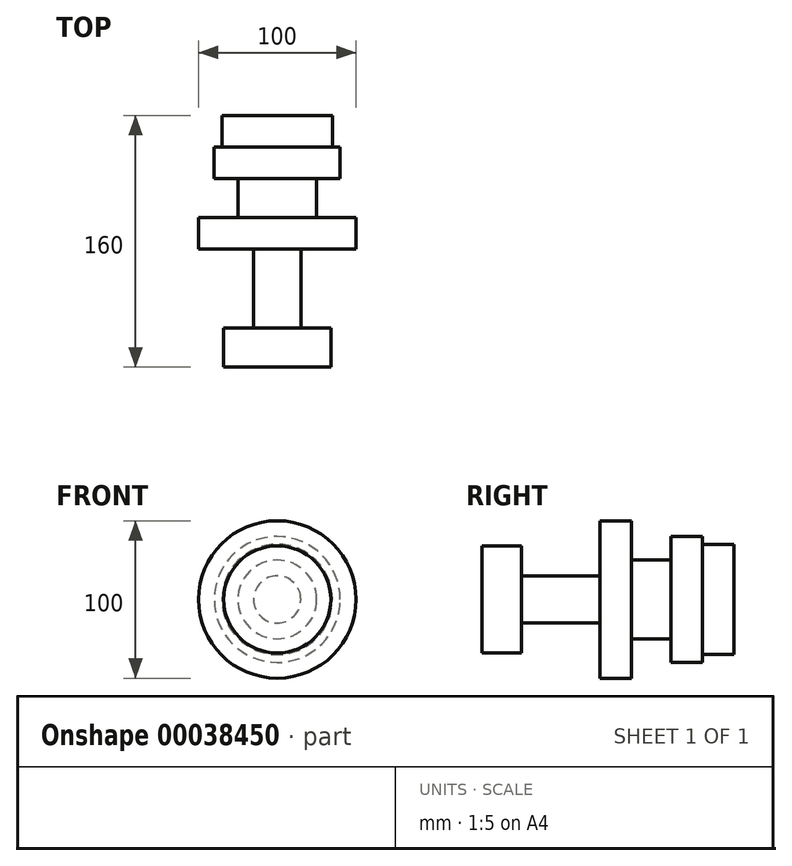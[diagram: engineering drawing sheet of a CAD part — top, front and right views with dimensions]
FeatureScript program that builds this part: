
annotation { "Feature Type Name" : "Feature", "Feature Type Description" : "" }
export const myFeature = defineFeature(function(context is Context, id is Id, definition is map)
    precondition{}
    {
        {
            var Q0;
            Q0=qCreatedBy(makeId("Front.planeOp"),FACE);
            var sketch = newSketch(context, id + "F0", { "sketchPlane" : qUnion([Q0])});
            skCircle(sketch, "E0", {"center": v(0, 0) * mm, "radius": 35 * mm});
            skSolve(sketch);
        }
        {
            var Q0;
            Q0=qSketchRegion(id+"F0",true);
            extrude(context, id + "F1", {"entities" : qUnion([Q0]), "depth" : 20 * mm});
        }
        {
            var Q0;
            Q0=makeQuery(id+"F1.opExtrude","CAP_FACE",FACE,{"disambiguationData":[OSD([sQuery(id+"F0.wireOp",EDGE,"E0")])],"isStart":false});
            var sketch = newSketch(context, id + "F2", { "sketchPlane" : qUnion([Q0])});
            skCircle(sketch, "E1", {"center": v(0, 0) * mm, "radius": 40 * mm});
            skSolve(sketch);
        }
        {
            var Q0;
            Q0=makeQuery(id+"F2.imprint","IMPRINT",FACE,{"disambiguationData":[TD([[makeQuery(id+"F2.imprint","IMPRINT",EDGE,{"derivedFrom":sQuery(id+"F2.wireOp",EDGE,"E1")}),1.0]])]});
            var Q1;
            Q1=makeQuery(id+"F2.imprint","IMPRINT",FACE,{"disambiguationData":[TD([[makeQuery(id+"F2.imprint","IMPRINT",EDGE,{"derivedFrom":makeQuery(id+"F1.opExtrude","CAP_EDGE",EDGE,{"disambiguationData":[OSD([sQuery(id+"F0.wireOp",EDGE,"E0")])],"isStart":false})}),1.0]])]});
            var Q2;
            Q2=sQuery(id+"F2.wireOp",EDGE,"E1");
            extrude(context, id + "F3", {"entities" : qUnion([Q0, Q1]), "surfaceEntities" : qUnion([Q2]), "depth" : 20 * mm});
        }
        {
            var Q0;
            Q0=makeQuery(id+"F3.opExtrude","CAP_FACE",FACE,{"disambiguationData":[OSD([sQuery(id+"F2.wireOp",EDGE,"E1")])],"isStart":false});
            var sketch = newSketch(context, id + "F4", { "sketchPlane" : qUnion([Q0])});
            skCircle(sketch, "E2", {"center": v(0, 0) * mm, "radius": 25 * mm});
            skSolve(sketch);
        }
        {
            var Q0;
            Q0=makeQuery(id+"F4.imprint","IMPRINT",FACE,{"disambiguationData":[TD([[makeQuery(id+"F4.imprint","IMPRINT",EDGE,{"derivedFrom":sQuery(id+"F4.wireOp",EDGE,"E2")}),1.0]])]});
            var Q1;
            Q1=sQuery(id+"F4.wireOp",EDGE,"E2");
            extrude(context, id + "F5", {"entities" : qUnion([Q0]), "operationType" : NewBodyOperationType.ADD, "surfaceEntities" : qUnion([Q1]), "depth" : 25 * mm});
        }
        {
            var Q0;
            Q0=makeQuery(id+"F5.opExtrude","CAP_FACE",FACE,{"disambiguationData":[OSD([sQuery(id+"F4.wireOp",EDGE,"E2")])],"isStart":false});
            var sketch = newSketch(context, id + "F6", { "sketchPlane" : qUnion([Q0])});
            skCircle(sketch, "E3", {"center": v(0, 0) * mm, "radius": 50 * mm});
            skSolve(sketch);
        }
        {
            var Q0;
            Q0=qSketchRegion(id+"F6",true);
            extrude(context, id + "F7", {"entities" : qUnion([Q0]), "operationType" : NewBodyOperationType.ADD, "depth" : 20 * mm});
        }
        {
            var Q0;
            Q0=makeQuery(id+"F7.opExtrude","CAP_FACE",FACE,{"disambiguationData":[OSD([sQuery(id+"F6.wireOp",EDGE,"E3")])],"isStart":false});
            var sketch = newSketch(context, id + "F8", { "sketchPlane" : qUnion([Q0])});
            skCircle(sketch, "E4", {"center": v(0, 0) * mm, "radius": 15 * mm});
            skSolve(sketch);
        }
        {
            var Q0;
            Q0=qSketchRegion(id+"F8",true);
            extrude(context, id + "F9", {"entities" : qUnion([Q0]), "operationType" : NewBodyOperationType.ADD, "depth" : 50 * mm});
        }
        {
            var Q0;
            Q0=makeQuery(id+"F9.opExtrude","CAP_FACE",FACE,{"disambiguationData":[OSD([sQuery(id+"F8.wireOp",EDGE,"E4")])],"isStart":false});
            var sketch = newSketch(context, id + "F10", { "sketchPlane" : qUnion([Q0])});
            skCircle(sketch, "E5", {"center": v(0, 0) * mm, "radius": 34.03 * mm});
            skSolve(sketch);
        }
        {
            var Q0;
            Q0=makeQuery(id+"F10.imprint","IMPRINT",FACE,{"disambiguationData":[TD([[makeQuery(id+"F10.imprint","IMPRINT",EDGE,{"derivedFrom":makeQuery(id+"F9.opExtrude","CAP_EDGE",EDGE,{"disambiguationData":[OSD([sQuery(id+"F8.wireOp",EDGE,"E4")])],"isStart":false})}),1.0]])]});
            var Q1;
            Q1=makeQuery(id+"F10.imprint","IMPRINT",FACE,{"disambiguationData":[TD([[makeQuery(id+"F10.imprint","IMPRINT",EDGE,{"derivedFrom":sQuery(id+"F10.wireOp",EDGE,"E5")}),1.0]])]});
            var Q2;
            Q2=sQuery(id+"F10.wireOp",EDGE,"E5");
            extrude(context, id + "F11", {"entities" : qUnion([Q0, Q1]), "operationType" : NewBodyOperationType.ADD, "surfaceEntities" : qUnion([Q2]), "depth" : 25 * mm});
        }
    });
